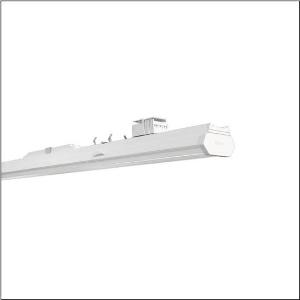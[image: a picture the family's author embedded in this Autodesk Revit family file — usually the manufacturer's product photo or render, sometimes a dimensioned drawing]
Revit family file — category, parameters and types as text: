
# Revit family: licross_r__11_protected_ho_51td11mn4gxs_4279
name_source: partatom
category: Lighting Fixtures
units: mm (PartAtom-declared; Revit-internal decimal feet)

## family parameters
Cut with Voids When Loaded = No
Host = Face
Light Source = No
Part Type = Normal
Room Calculation Point = No
Round Connector Dimension = Use Diameter
Shared = No

## types (1)
- --- (1 x LED, 16070 lm, 87.4 W, 4000K)
    Apparent Load = 87 VA
    CIE Flux Codes = 84 94 98 99 100
    Color Rendering = 80
    Color Temperature = 4000K
    Default Elevation = 1800 mm
    Description = Licross® 11 Protected HO, luminaire insert, of sheet steel, galvanised, coil coated, white, length: 1.500mm, width: 90mm, height: 101mm, LED rated luminous flux: 16.070lm, light colour: 840, control gear: ON/OFF Multilumen, with plug, 3-pole, with phase selection, mains connection: 220..240V, AC, 50/60Hz, rated input power: 87W, halogen-free wiring, primary light control with lens, of plastic, primary optical cover: cover, of PMMA, light emission: direct distribution, primary light characteristic: symmetric, protection rating (complete): IP54, insulation class (complete): insulation class I (protective earthing), certification: CE, ENEC, VDE, UKCA, protection symbol: D if used in an environment with non-conductive dust loads with corresponding accessories, impact resistance: IK06, permissible ambient temperature for indoor applications: -35..+35°C, corresponds to IFS (International Featured Standards) requirements for safety and quality in the food industry, reducing of maximum allowable ambient temperature of 5°C with ceiling mounting, LABS conformity tested according to VDMA 24364:2018-05, packaging unit: 1 piece
    Height = 92 mm
    Lamp = 1 x LED
    Lamp Light Flux = 16070 lm
    Lamp Power = 87.4 W
    Lamp count = 1
    Length = 1500 mm
    Luminous efficacy = 184 lm/W
    Manufacturer = Siteco
    ModVariant = No
    Model = 51TD11MN4GXS
    Mounting Place = Ceiling
    Mounting Type = Pendant
    Number of Poles = 1
    OnlyDefault = Yes
    Power Factor = 1
    Product Name = Licross® 11 Protected HO
    Product group = luminaire insert
    ProductGroupID = 901
    Protection Class = Protection class I
    Protection Degree = IP 54
    RLX_Detail_Level = 1
    RLX_Emergency_Light_Flux = 0 lm
    RLX_Emergency_Type = 0
    RLX_Emergency_Type_DB = No
    RlxData = <blob elided: 21965 chars, md5=a0b75fca>
    Socket = socket
    Standby Power = 0 W
    System Light Flux = 16070 lm
    System Power = 87 W
    Type Comments = factory setting: luminous flux: 100 % | (A | C | E) | 203 mA
    Type Image = l_1256145.jpg
    URL = http://relux.com
    VarID = @adj_038057
    Voltage = 0 V
    Weight = 0.00 kg
    Width = 88 mm

## geometry (parser evidence)
native form markers: Blend x4, Sweep x13
no freeform markers — native parametric forms only
